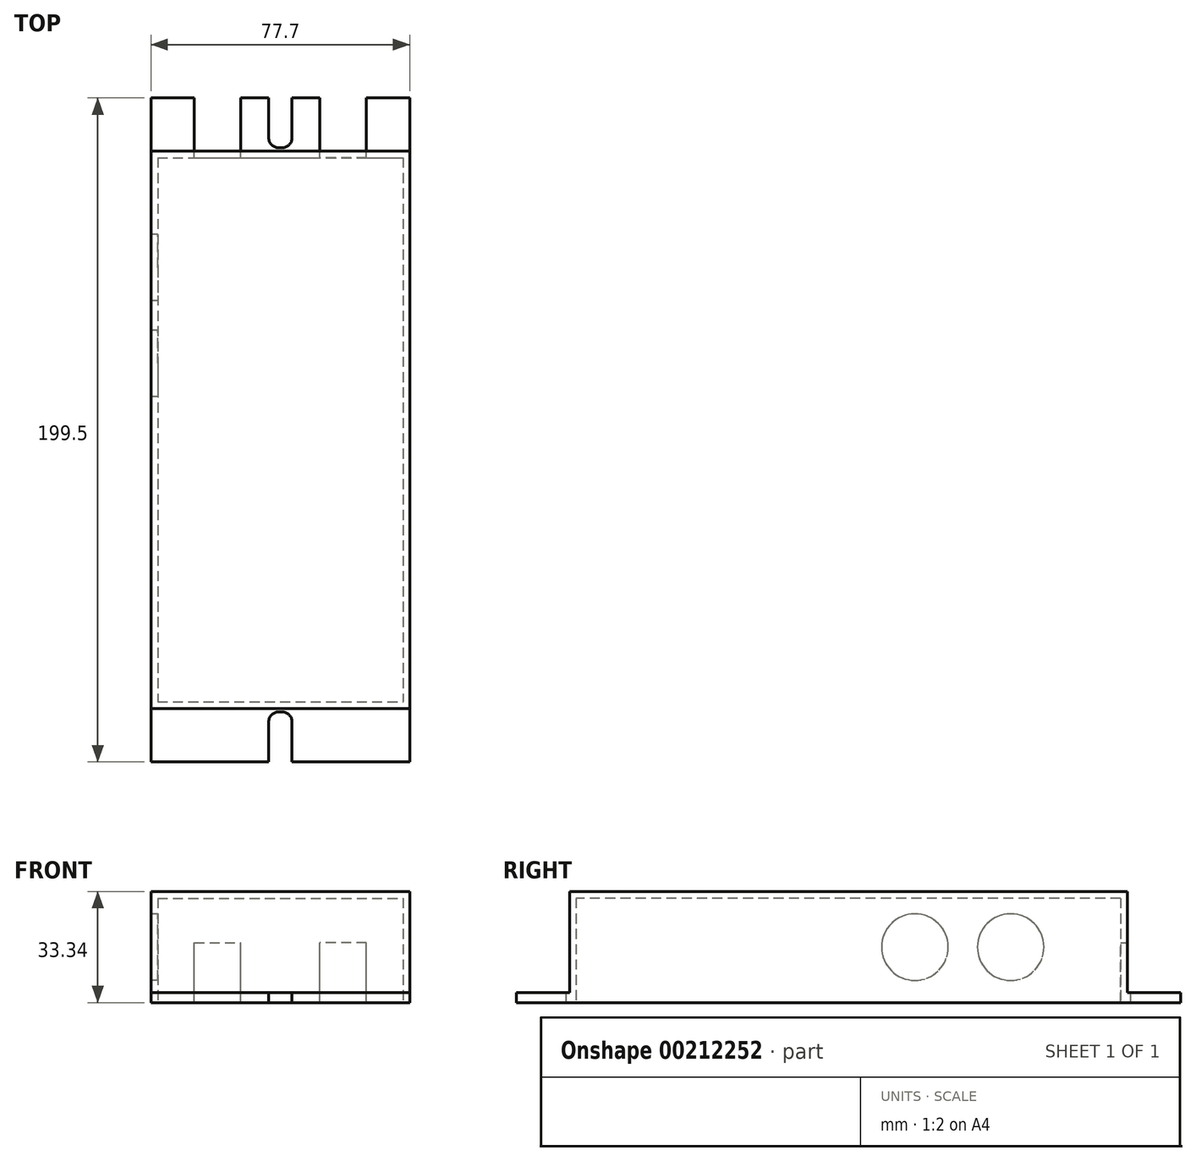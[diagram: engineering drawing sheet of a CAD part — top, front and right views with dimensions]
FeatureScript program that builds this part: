
annotation { "Feature Type Name" : "Feature", "Feature Type Description" : "" }
export const myFeature = defineFeature(function(context is Context, id is Id, definition is map)
    precondition{}
    {
        {
            var Q0;
            Q0=qCreatedBy(makeId("Top.planeOp"),FACE);
            var sketch = newSketch(context, id + "F0", { "sketchPlane" : qUnion([Q0])});
            skLineSegment(sketch, "E0.bottom", {"start": v(-38.85, 83.75) * mm, "end": v(38.85, 83.75) * mm});
            skLineSegment(sketch, "E0.top", {"start": v(-38.85, -83.75) * mm, "end": v(38.85, -83.75) * mm});
            skLineSegment(sketch, "E0.left", {"start": v(-38.85, 83.75) * mm, "end": v(-38.85, -83.75) * mm});
            skLineSegment(sketch, "E0.right", {"start": v(38.85, 83.75) * mm, "end": v(38.85, -83.75) * mm});
            skPoint(sketch, "E0.middle", {"position": v(0, 0) * mm});
            skSolve(sketch);
        }
        {
            var Q0;
            Q0=makeQuery(id+"F0.imprint","IMPRINT",FACE,{"disambiguationData":[TD([[makeQuery(id+"F0.imprint","IMPRINT",EDGE,{"derivedFrom":sQuery(id+"F0.wireOp",EDGE,"E0.bottom")}),-1.0]])]});
            extrude(context, id + "F1", {"entities" : qUnion([Q0]), "depth" : 33.34 * mm});
        }
        {
            var Q0;
            Q0=makeQuery(id+"F1.opExtrude","CAP_FACE",FACE,{"disambiguationData":[OSD([sQuery(id+"F0.wireOp",EDGE,"E0.bottom"),sQuery(id+"F0.wireOp",EDGE,"E0.top"),sQuery(id+"F0.wireOp",EDGE,"E0.left"),sQuery(id+"F0.wireOp",EDGE,"E0.right")])],"isStart":true});
            shell(context, id + "F2", {"entities" : qUnion([Q0]), "thickness" : 2 * mm});
        }
        {
            var Q0;
            Q0=makeQuery(id+"F1.opExtrude","SWEPT_FACE",FACE,{"disambiguationData":[OSD([sQuery(id+"F0.wireOp",EDGE,"E0.left")])]});
            var sketch = newSketch(context, id + "F3", { "sketchPlane" : qUnion([Q0])});
            skCircle(sketch, "E1", {"center": v(-48.75, 16.67) * mm, "radius": 10 * mm});
            skCircle(sketch, "E2", {"center": v(-19.98, 16.67) * mm, "radius": 10 * mm});
            skSolve(sketch);
        }
        {
            var Q0;
            Q0=makeQuery(id+"F3.imprint","IMPRINT",FACE,{"disambiguationData":[TD([[makeQuery(id+"F3.imprint","IMPRINT",EDGE,{"derivedFrom":sQuery(id+"F3.wireOp",EDGE,"E2")}),1.0]])]});
            var Q1;
            Q1=makeQuery(id+"F3.imprint","IMPRINT",FACE,{"disambiguationData":[TD([[makeQuery(id+"F3.imprint","IMPRINT",EDGE,{"derivedFrom":sQuery(id+"F3.wireOp",EDGE,"E1")}),1.0]])]});
            extrude(context, id + "F4", {"entities" : qUnion([Q0, Q1]), "operationType" : NewBodyOperationType.REMOVE, "oppositeDirection" : true, "depth" : 25 * mm});
        }
        {
            var Q0;
            Q0=makeQuery(id+"F1.opExtrude","CAP_FACE",FACE,{"disambiguationData":[OSD([sQuery(id+"F0.wireOp",EDGE,"E0.bottom"),sQuery(id+"F0.wireOp",EDGE,"E0.top"),sQuery(id+"F0.wireOp",EDGE,"E0.left"),sQuery(id+"F0.wireOp",EDGE,"E0.right")])],"isStart":true});
            var sketch = newSketch(context, id + "F5", { "sketchPlane" : qUnion([Q0])});
            skLineSegment(sketch, "E3.bottom", {"start": v(-38.85, 83.75) * mm, "end": v(38.85, 83.75) * mm});
            skLineSegment(sketch, "E3.top", {"start": v(-38.85, 99.75) * mm, "end": v(38.85, 99.75) * mm});
            skLineSegment(sketch, "E3.left", {"start": v(-38.85, 83.75) * mm, "end": v(-38.85, 99.75) * mm});
            skLineSegment(sketch, "E3.right", {"start": v(38.85, 83.75) * mm, "end": v(38.85, 99.75) * mm});
            skSolve(sketch);
        }
        {
            var Q0;
            Q0 = qSketchRegion(id + "F5", true);
            extrude(context, id + "F6", {"entities" : qUnion([Q0]), "operationType" : NewBodyOperationType.ADD, "oppositeDirection" : true, "depth" : 3 * mm});
        }
        {
            var Q0;
            Q0=makeQuery(id+"F6.opExtrude","CAP_FACE",FACE,{"disambiguationData":[OSD([sQuery(id+"F5.wireOp",EDGE,"E3.bottom"),sQuery(id+"F5.wireOp",EDGE,"E3.top"),sQuery(id+"F5.wireOp",EDGE,"E3.left"),sQuery(id+"F5.wireOp",EDGE,"E3.right")])],"isStart":false});
            var sketch = newSketch(context, id + "F7", { "sketchPlane" : qUnion([Q0])});
            skLineSegment(sketch, "E4.bottom", {"start": v(-3.5, -99.75) * mm, "end": v(3.5, -99.75) * mm});
            skLineSegment(sketch, "E4.top", {"start": v(-0.5, -84.75) * mm, "end": v(0.5, -84.75) * mm});
            skLineSegment(sketch, "E4.left", {"start": v(-3.5, -99.75) * mm, "end": v(-3.5, -87.75) * mm});
            skLineSegment(sketch, "E4.right", {"start": v(3.5, -99.75) * mm, "end": v(3.5, -87.75) * mm});
            skPoint(sketch, "E5.visualSharp", {"position": v(-3.5, -84.75) * mm});
            skArc(sketch, "E5.filletArc", {"start": v(-0.5, -84.75) * mm, "mid": v(-2.62, -85.63) * mm, "end": v(-3.5, -87.75) * mm});
            skPoint(sketch, "E6.visualSharp", {"position": v(3.5, -84.75) * mm});
            skArc(sketch, "E6.filletArc", {"start": v(3.5, -87.75) * mm, "mid": v(2.62, -85.63) * mm, "end": v(0.5, -84.75) * mm});
            skSolve(sketch);
        }
        {
            var Q0;
            Q0 = qSketchRegion(id + "F7", true);
            extrude(context, id + "F8", {"entities" : qUnion([Q0]), "operationType" : NewBodyOperationType.REMOVE, "oppositeDirection" : true, "depth" : 25 * mm});
        }
        {
            var Q0;
            Q0=makeQuery(id+"F6.boolean.opBoolean","MERGE",FACE,{"derivedFrom":[makeQuery(id+"F1.opExtrude","CAP_FACE",FACE,{"disambiguationData":[OSD([sQuery(id+"F0.wireOp",EDGE,"E0.bottom"),sQuery(id+"F0.wireOp",EDGE,"E0.top"),sQuery(id+"F0.wireOp",EDGE,"E0.left"),sQuery(id+"F0.wireOp",EDGE,"E0.right")])],"isStart":true}),makeQuery(id+"F6.opExtrude","CAP_FACE",FACE,{"disambiguationData":[OSD([sQuery(id+"F5.wireOp",EDGE,"E3.bottom"),sQuery(id+"F5.wireOp",EDGE,"E3.top"),sQuery(id+"F5.wireOp",EDGE,"E3.left"),sQuery(id+"F5.wireOp",EDGE,"E3.right")])],"isStart":true})]});
            var sketch = newSketch(context, id + "F9", { "sketchPlane" : qUnion([Q0])});
            skLineSegment(sketch, "E7.bottom", {"start": v(-38.85, -83.75) * mm, "end": v(38.85, -83.75) * mm});
            skLineSegment(sketch, "E7.top", {"start": v(-38.85, -99.75) * mm, "end": v(38.85, -99.75) * mm});
            skLineSegment(sketch, "E7.left", {"start": v(-38.85, -83.75) * mm, "end": v(-38.85, -99.75) * mm});
            skLineSegment(sketch, "E7.right", {"start": v(38.85, -83.75) * mm, "end": v(38.85, -99.75) * mm});
            skSolve(sketch);
        }
        {
            var Q0;
            Q0=makeQuery(id+"F9.imprint","IMPRINT",FACE,{"disambiguationData":[TD([[makeQuery(id+"F9.imprint","IMPRINT",EDGE,{"derivedFrom":sQuery(id+"F9.wireOp",EDGE,"E7.bottom")}),-1.0]])]});
            extrude(context, id + "F10", {"entities" : qUnion([Q0]), "operationType" : NewBodyOperationType.ADD, "oppositeDirection" : true, "depth" : 3 * mm});
        }
        {
            var Q0;
            Q0=makeQuery(id+"F10.boolean.opBoolean","MERGE",FACE,{"derivedFrom":[makeQuery(id+"F6.boolean.opBoolean","MERGE",FACE,{"derivedFrom":[makeQuery(id+"F1.opExtrude","CAP_FACE",FACE,{"disambiguationData":[OSD([sQuery(id+"F0.wireOp",EDGE,"E0.bottom"),sQuery(id+"F0.wireOp",EDGE,"E0.top"),sQuery(id+"F0.wireOp",EDGE,"E0.left"),sQuery(id+"F0.wireOp",EDGE,"E0.right")])],"isStart":true}),makeQuery(id+"F6.opExtrude","CAP_FACE",FACE,{"disambiguationData":[OSD([sQuery(id+"F5.wireOp",EDGE,"E3.bottom"),sQuery(id+"F5.wireOp",EDGE,"E3.top"),sQuery(id+"F5.wireOp",EDGE,"E3.left"),sQuery(id+"F5.wireOp",EDGE,"E3.right")])],"isStart":true})]}),makeQuery(id+"F10.opExtrude","CAP_FACE",FACE,{"disambiguationData":[OSD([sQuery(id+"F9.wireOp",EDGE,"E7.bottom"),sQuery(id+"F9.wireOp",EDGE,"E7.top"),sQuery(id+"F9.wireOp",EDGE,"E7.left"),sQuery(id+"F9.wireOp",EDGE,"E7.right")])],"isStart":true})]});
            var sketch = newSketch(context, id + "F11", { "sketchPlane" : qUnion([Q0])});
            skLineSegment(sketch, "E8.bottom", {"start": v(-3.5, -99.75) * mm, "end": v(3.5, -99.75) * mm});
            skLineSegment(sketch, "E8.top", {"start": v(-0.5, -84.75) * mm, "end": v(0.5, -84.75) * mm});
            skLineSegment(sketch, "E8.left", {"start": v(-3.5, -99.75) * mm, "end": v(-3.5, -87.75) * mm});
            skLineSegment(sketch, "E8.right", {"start": v(3.5, -99.75) * mm, "end": v(3.5, -87.75) * mm});
            skPoint(sketch, "E9.visualSharp", {"position": v(-3.5, -84.75) * mm});
            skArc(sketch, "E9.filletArc", {"start": v(-0.5, -84.75) * mm, "mid": v(-2.62, -85.63) * mm, "end": v(-3.5, -87.75) * mm});
            skPoint(sketch, "E10.visualSharp", {"position": v(3.5, -84.75) * mm});
            skArc(sketch, "E10.filletArc", {"start": v(3.5, -87.75) * mm, "mid": v(2.62, -85.63) * mm, "end": v(0.5, -84.75) * mm});
            skSolve(sketch);
        }
        {
            var Q0;
            Q0 = qSketchRegion(id + "F11", true);
            extrude(context, id + "F12", {"entities" : qUnion([Q0]), "operationType" : NewBodyOperationType.REMOVE, "oppositeDirection" : true, "depth" : 25 * mm});
        }
        {
            var Q0;
            {var subQ1=sQuery(id+"F0.wireOp",EDGE,"E0.right");var subQ4=sQuery(id+"F9.wireOp",EDGE,"E7.top");Q0=makeQuery(id+"F12.boolean.opBoolean","SPLIT",FACE,{"disambiguationData":[TD([makeQuery(id+"F1.opExtrude","SWEPT_FACE",FACE,{"disambiguationData":[OSD([subQ1])]})])],"derivedFrom":makeQuery(id+"F10.opExtrude","SWEPT_FACE",FACE,{"disambiguationData":[OSD([subQ4])]})});}
            var sketch = newSketch(context, id + "F13", { "sketchPlane" : qUnion([Q0])});
            skLineSegment(sketch, "E11.bottom", {"start": v(-25.85, 0) * mm, "end": v(-11.85, 0) * mm});
            skLineSegment(sketch, "E11.top", {"start": v(-25.85, 18) * mm, "end": v(-11.85, 18) * mm});
            skLineSegment(sketch, "E11.left", {"start": v(-25.85, 0) * mm, "end": v(-25.85, 18) * mm});
            skLineSegment(sketch, "E11.right", {"start": v(-11.85, 0) * mm, "end": v(-11.85, 18) * mm});
            skLineSegment(sketch, "E12.MirrorCS", {"start": v(25.85, 0) * mm, "end": v(11.85, 0) * mm});
            skLineSegment(sketch, "E13.MirrorCS", {"start": v(25.85, 18) * mm, "end": v(11.85, 18) * mm});
            skLineSegment(sketch, "E14.MirrorCS", {"start": v(11.85, 0) * mm, "end": v(11.85, 18) * mm});
            skLineSegment(sketch, "E15.MirrorCS", {"start": v(25.85, 0) * mm, "end": v(25.85, 18) * mm});
            skSolve(sketch);
        }
        {
            var Q0;
            Q0=makeQuery(id+"F13.imprint","IMPRINT",FACE,{"disambiguationData":[TD([[makeQuery(id+"F13.imprint","IMPRINT",EDGE,{"derivedFrom":sQuery(id+"F13.wireOp",EDGE,"E12.MirrorCS")}),-1.0]])]});
            var Q1;
            {var subQ0=sQuery(id+"F13.wireOp",EDGE,"E11.top");Q1=makeQuery(id+"F13.imprint","IMPRINT",FACE,{"disambiguationData":[TD([[makeQuery(id+"F13.imprint","IMPRINT",EDGE,{"derivedFrom":subQ0}),-1.0]])]});}
            var Q2;
            {var subQ0=sQuery(id+"F13.wireOp",EDGE,"E11.bottom");Q2=makeQuery(id+"F13.imprint","IMPRINT",FACE,{"disambiguationData":[TD([[makeQuery(id+"F13.imprint","IMPRINT",EDGE,{"derivedFrom":subQ0}),-1.0]])]});}
            extrude(context, id + "F14", {"entities" : qUnion([Q0, Q1, Q2]), "operationType" : NewBodyOperationType.REMOVE, "oppositeDirection" : true, "depth" : 25 * mm});
        }
    });
